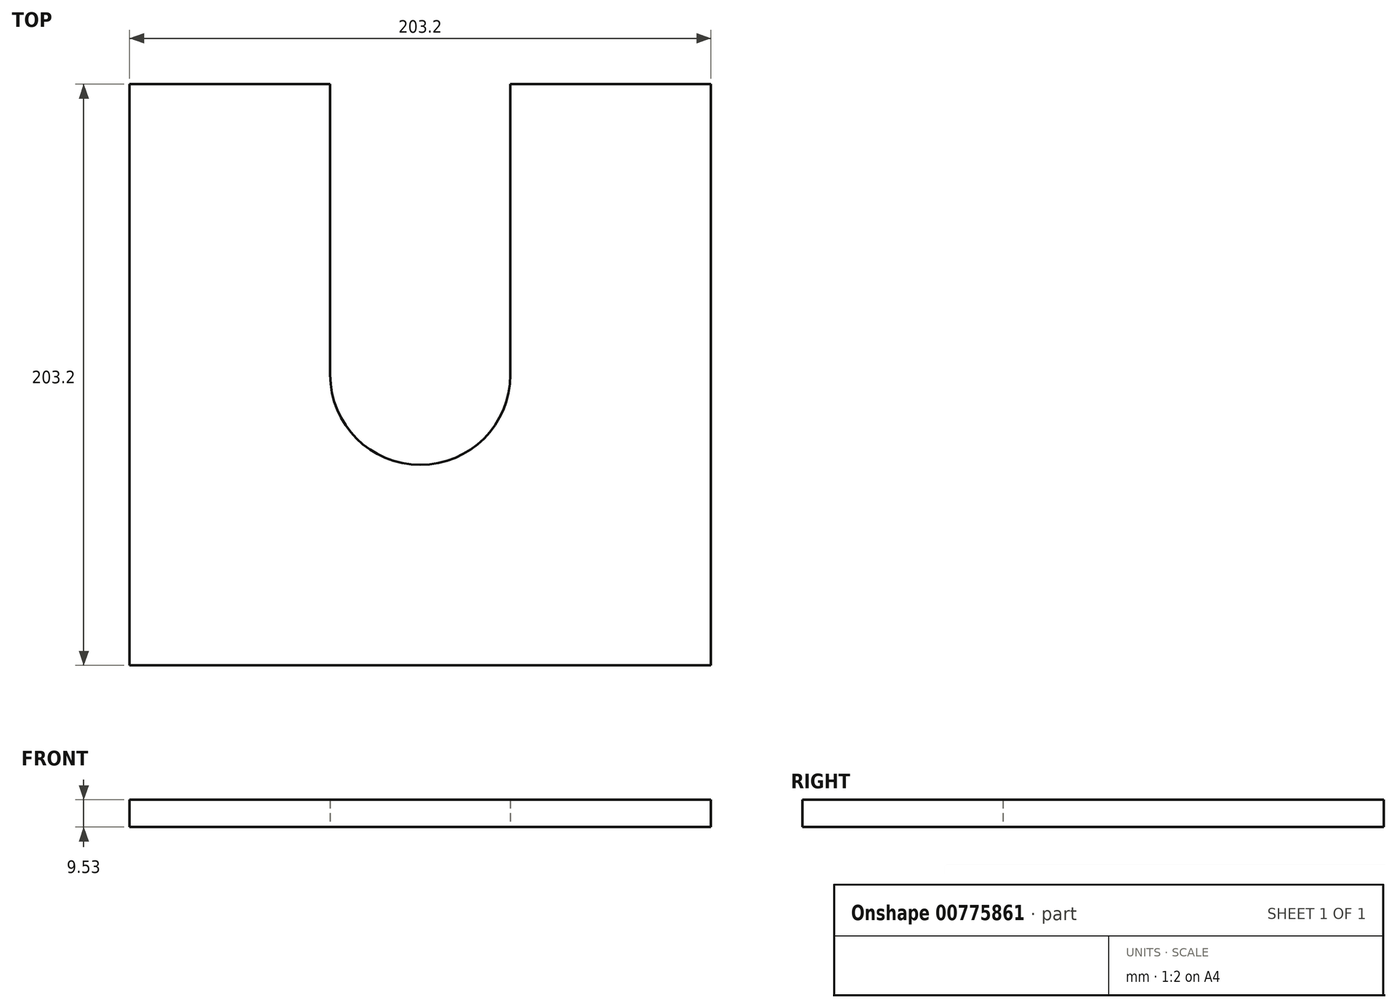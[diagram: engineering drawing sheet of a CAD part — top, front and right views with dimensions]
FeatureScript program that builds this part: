
annotation { "Feature Type Name" : "Feature", "Feature Type Description" : "" }
export const myFeature = defineFeature(function(context is Context, id is Id, definition is map)
    precondition{}
    {
        {
            var Q0;
            Q0=qCreatedBy(makeId("Top.planeOp"),FACE);
            var sketch = newSketch(context, id + "F0", { "sketchPlane" : qUnion([Q0])});
            skLineSegment(sketch, "E0.top", {"start": v(-101.6, -101.6) * mm, "end": v(101.6, -101.6) * mm});
            skLineSegment(sketch, "E0.left", {"start": v(-101.6, 101.6) * mm, "end": v(-101.6, -101.6) * mm});
            skLineSegment(sketch, "E0.right", {"start": v(101.6, 101.6) * mm, "end": v(101.6, -101.6) * mm});
            skPoint(sketch, "E0.middle", {"position": v(0, 0) * mm});
            skCircle(sketch, "E1", {"center": v(0, 0) * mm, "radius": 31.5 * mm, "construction": true});
            skLineSegment(sketch, "E2", {"start": v(-101.6, 101.6) * mm, "end": v(-31.5, 101.6) * mm});
            skLineSegment(sketch, "E3", {"start": v(31.5, 101.6) * mm, "end": v(101.6, 101.6) * mm});
            skLineSegment(sketch, "E4", {"start": v(-31.5, 0) * mm, "end": v(-31.5, 101.6) * mm});
            skLineSegment(sketch, "E5", {"start": v(31.5, 0) * mm, "end": v(31.5, 101.6) * mm});
            skArc(sketch, "E6", {"start": v(-31.5, 0) * mm, "mid": v(0, -31.5) * mm, "end": v(31.5, 0) * mm});
            skSolve(sketch);
        }
        {
            var Q0;
            Q0=makeQuery(id+"F0.imprint","IMPRINT",FACE,{"disambiguationData":[TD([[makeQuery(id+"F0.imprint","IMPRINT",EDGE,{"derivedFrom":sQuery(id+"F0.wireOp",EDGE,"E0.top")}),1.0]])]});
            extrude(context, id + "F1", {"entities" : qUnion([Q0]), "depth" : 9.52 * mm, "offsetDistance" : 25.4 * mm});
        }
    });
